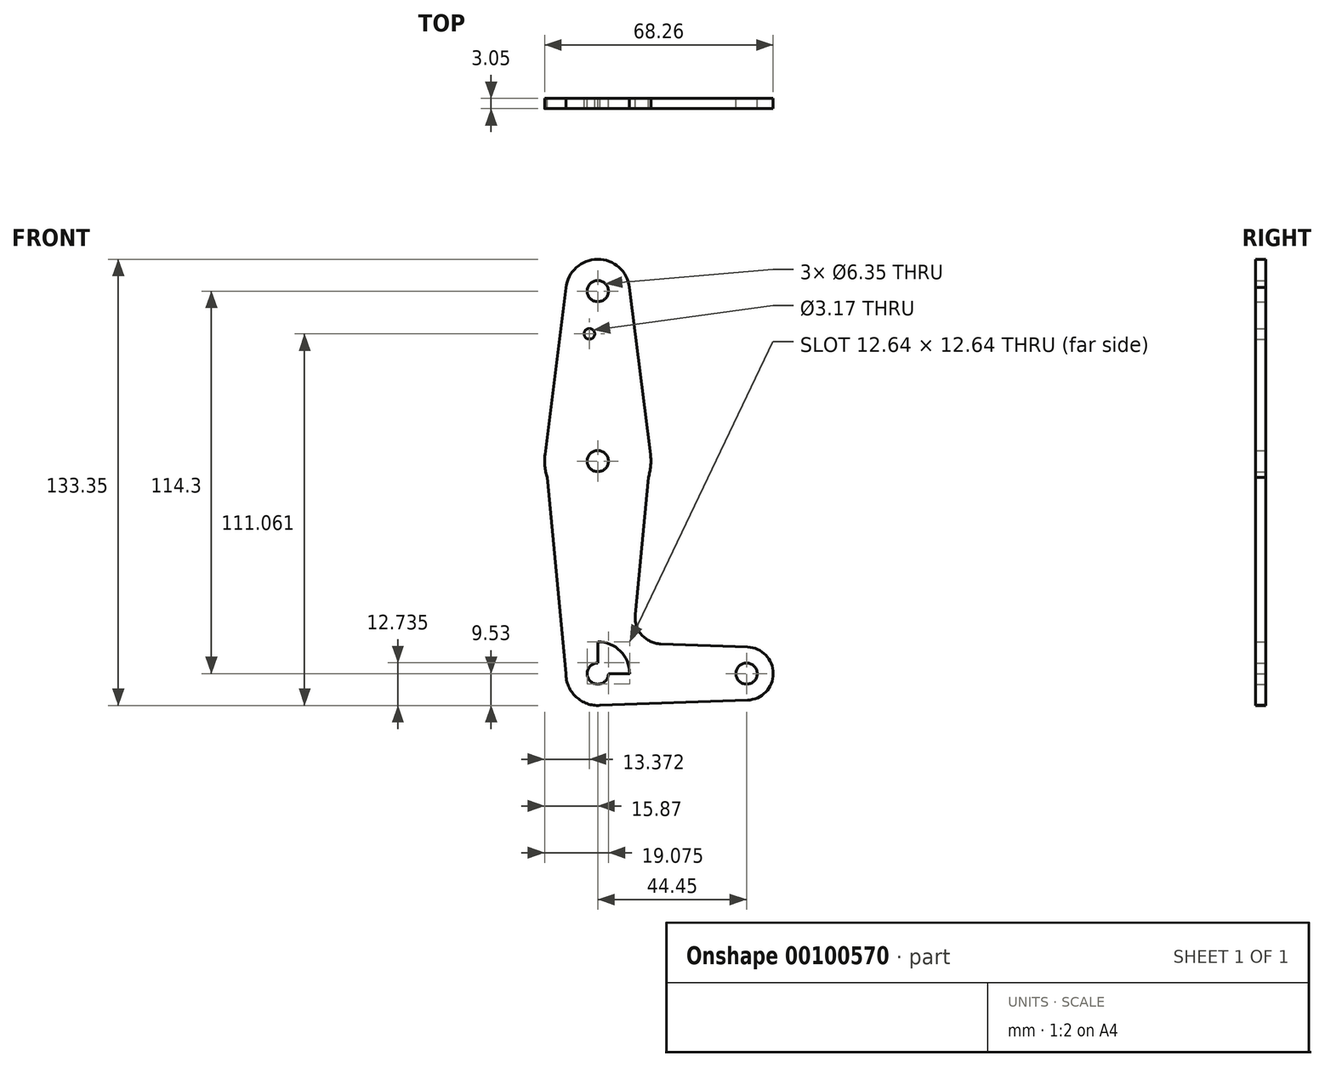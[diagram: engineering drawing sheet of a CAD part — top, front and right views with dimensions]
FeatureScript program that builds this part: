
annotation { "Feature Type Name" : "Feature", "Feature Type Description" : "" }
export const myFeature = defineFeature(function(context is Context, id is Id, definition is map)
    precondition{}
    {
        {
            var Q0;
            Q0=qCreatedBy(makeId("Front.planeOp"),FACE);
            var sketch = newSketch(context, id + "F0", { "sketchPlane" : qUnion([Q0])});
            skLineSegment(sketch, "E0", {"start": v(0, 0) * mm, "end": v(0, 114.3) * mm});
            skLineSegment(sketch, "E1", {"start": v(0, 114.3) * mm, "end": v(0, 0) * mm});
            skLineSegment(sketch, "E2", {"start": v(44.45, 0) * mm, "end": v(0, 0) * mm});
            skCircle(sketch, "E3", {"center": v(0, 114.3) * mm, "radius": 9.53 * mm});
            skCircle(sketch, "E4", {"center": v(0, 63.5) * mm, "radius": 15.88 * mm});
            skCircle(sketch, "E5", {"center": v(0, 0) * mm, "radius": 9.53 * mm});
            skCircle(sketch, "E6", {"center": v(44.45, 0) * mm, "radius": 7.94 * mm});
            skLineSegment(sketch, "E7", {"start": v(18.83, 8.85) * mm, "end": v(44.73, 7.93) * mm});
            skLineSegment(sketch, "E8", {"start": v(0, -9.53) * mm, "end": v(44.73, -7.93) * mm});
            skLineSegment(sketch, "E9", {"start": v(-9.47, 115.29) * mm, "end": v(-15.75, 65.49) * mm});
            skLineSegment(sketch, "E10", {"start": v(9.43, 115.6) * mm, "end": v(15.75, 65.48) * mm});
            skLineSegment(sketch, "E11", {"start": v(-15.75, 65.49) * mm, "end": v(-9.52, 0) * mm});
            skLineSegment(sketch, "E12", {"start": v(15.75, 65.48) * mm, "end": v(11.2, 17.55) * mm});
            skCircle(sketch, "E13", {"center": v(0, 0) * mm, "radius": 3.18 * mm});
            skCircle(sketch, "E14", {"center": v(0, 63.5) * mm, "radius": 3.18 * mm});
            skCircle(sketch, "E15", {"center": v(44.45, 0) * mm, "radius": 3.18 * mm});
            skCircle(sketch, "E16", {"center": v(0, 114.3) * mm, "radius": 3.18 * mm});
            skCircle(sketch, "E17", {"center": v(-2.5, 101.53) * mm, "radius": 1.59 * mm});
            skArc(sketch, "E18.filletArc", {"start": v(11.2, 17.55) * mm, "mid": v(13.13, 11.56) * mm, "end": v(18.83, 8.85) * mm});
            skSolve(sketch);
        }
        {
            var Q0;
            Q0 = qSketchRegion(id + "F0", true);
            var Q1;
            {var subQ0=sQuery(id+"F0.wireOp",EDGE,"E5");var subQ1=sQuery(id+"F0.wireOp",EDGE,"E1");var subQ2=makeQuery(id+"F0.imprint","INTERSECT",VERTEX,{"derivedFrom":[subQ1,subQ0]});Q1=makeQuery(id+"F0.imprint","IMPRINT",FACE,{"disambiguationData":[TD([[makeQuery(id+"F0.imprint","IMPRINT",EDGE,{"disambiguationData":[TD([[subQ2,-1.0]])],"derivedFrom":subQ1}),1.0]])]});}
            extrude(context, id + "F1", {"entities" : qUnion([Q0, Q1]), "depth" : 3.05 * mm});
        }
    });
